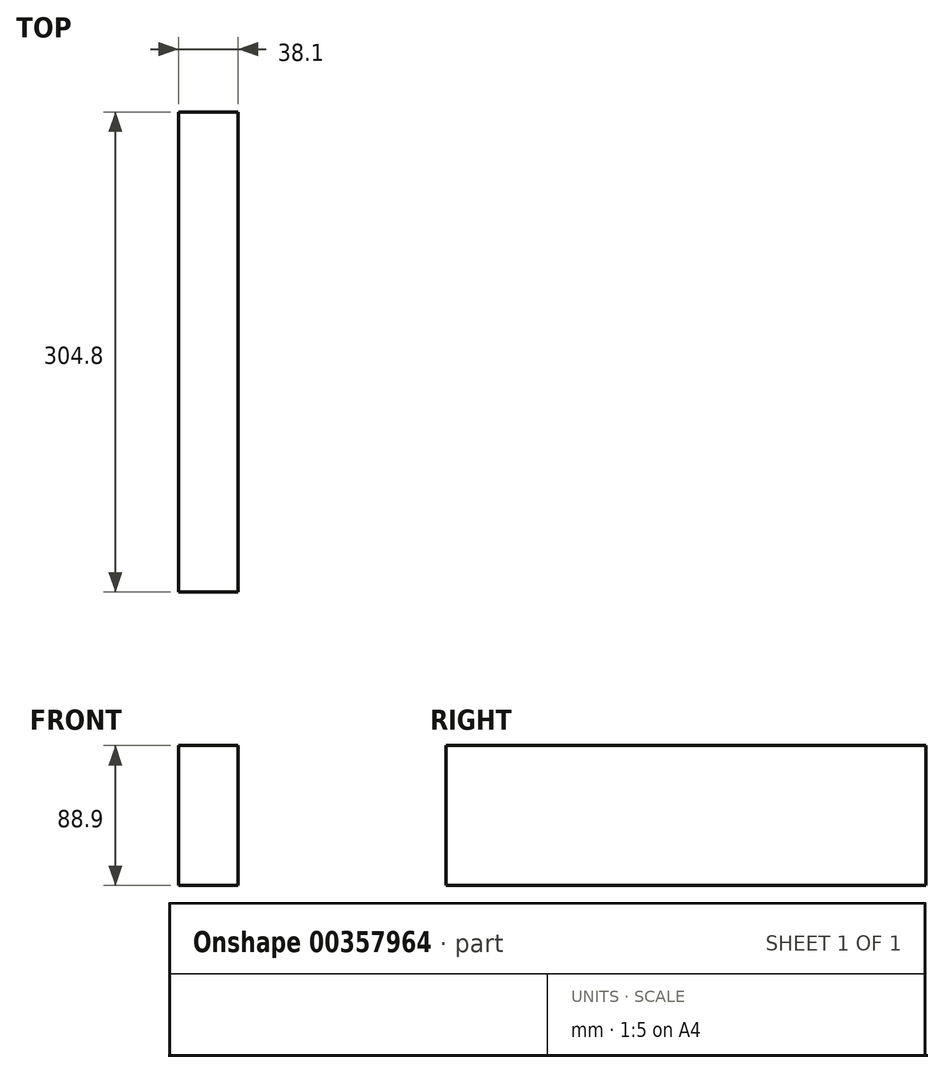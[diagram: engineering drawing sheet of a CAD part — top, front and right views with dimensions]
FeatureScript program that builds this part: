
annotation { "Feature Type Name" : "Feature", "Feature Type Description" : "" }
export const myFeature = defineFeature(function(context is Context, id is Id, definition is map)
    precondition{}
    {
        {
            var Q0;
            Q0=qCreatedBy(makeId("Front.planeOp"),FACE);
            var sketch = newSketch(context, id + "F0", { "sketchPlane" : qUnion([Q0])});
            skLineSegment(sketch, "E0.bottom", {"start": v(19.05, 44.45) * mm, "end": v(-19.05, 44.45) * mm});
            skLineSegment(sketch, "E0.top", {"start": v(19.05, -44.45) * mm, "end": v(-19.05, -44.45) * mm});
            skLineSegment(sketch, "E0.left", {"start": v(19.05, 44.45) * mm, "end": v(19.05, -44.45) * mm});
            skLineSegment(sketch, "E0.right", {"start": v(-19.05, 44.45) * mm, "end": v(-19.05, -44.45) * mm});
            skPoint(sketch, "E0.middle", {"position": v(0, 0) * mm});
            skSolve(sketch);
        }
        {
            var Q0;
            Q0=makeQuery(id+"F0.imprint","IMPRINT",FACE,{"disambiguationData":[TD([[makeQuery(id+"F0.imprint","IMPRINT",EDGE,{"derivedFrom":sQuery(id+"F0.wireOp",EDGE,"E0.bottom")}),1.0]])]});
            extrude(context, id + "F1", {"entities" : qUnion([Q0]), "depth" : 304.8 * mm, "symmetric" : true});
        }
    });
